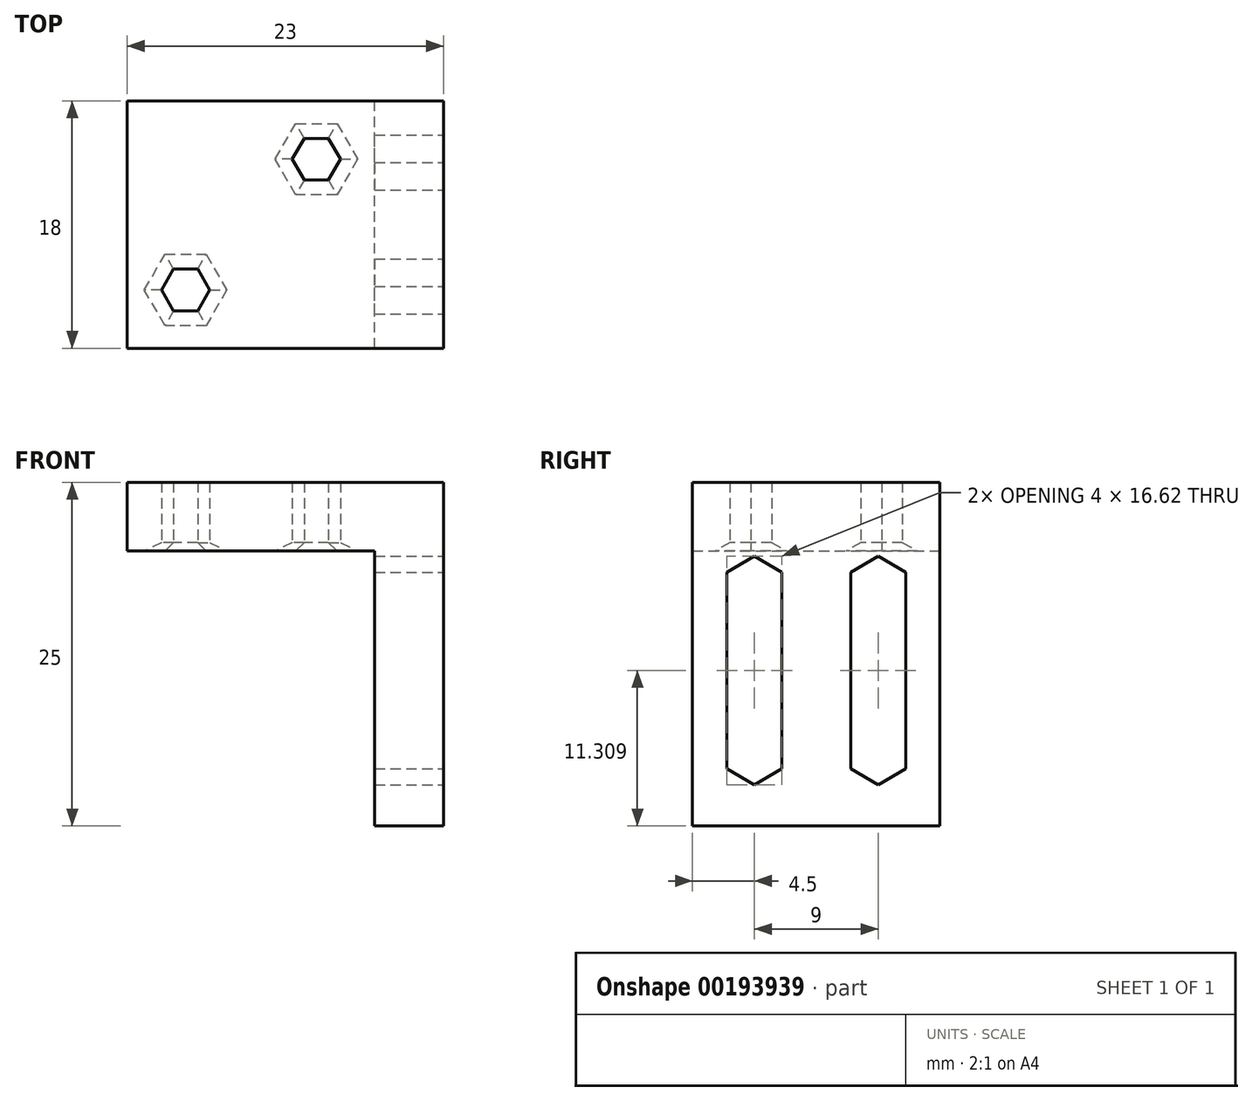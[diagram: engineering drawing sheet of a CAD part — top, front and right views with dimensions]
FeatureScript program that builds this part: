
annotation { "Feature Type Name" : "Feature", "Feature Type Description" : "" }
export const myFeature = defineFeature(function(context is Context, id is Id, definition is map)
    precondition{}
    {
        {
            var Q0;
            Q0=qCreatedBy(makeId("Front.planeOp"),FACE);
            var sketch = newSketch(context, id + "F0", { "sketchPlane" : qUnion([Q0])});
            skLineSegment(sketch, "E0", {"start": v(0, 0) * mm, "end": v(0, 20) * mm});
            skLineSegment(sketch, "E1", {"start": v(0, 20) * mm, "end": v(-18, 20) * mm});
            skLineSegment(sketch, "E2", {"start": v(-18, 20) * mm, "end": v(-18, 25) * mm});
            skLineSegment(sketch, "E3", {"start": v(-18, 25) * mm, "end": v(5, 25) * mm});
            skLineSegment(sketch, "E4", {"start": v(5, 25) * mm, "end": v(5, 0) * mm});
            skLineSegment(sketch, "E5", {"start": v(5, 0) * mm, "end": v(0, 0) * mm});
            skSolve(sketch);
        }
        {
            var Q0;
            Q0 = qSketchRegion(id + "F0", true);
            extrude(context, id + "F1", {"entities" : qUnion([Q0]), "depth" : 18 * mm});
        }
        {
            var Q0;
            Q0=makeQuery(id+"F1.opExtrude","SWEPT_FACE",FACE,{"disambiguationData":[OSD([sQuery(id+"F0.wireOp",EDGE,"E4")])]});
            var sketch = newSketch(context, id + "F2", { "sketchPlane" : qUnion([Q0])});
            skLineSegment(sketch, "E6", {"start": v(-9, 25) * mm, "end": v(-9, 0) * mm, "construction": true});
            skLineSegment(sketch, "E7", {"start": v(-13.5, 17.3) * mm, "end": v(-13.5, 5.3) * mm, "construction": true});
            skLineSegment(sketch, "E8", {"start": v(-18, 12.5) * mm, "end": v(-9, 12.5) * mm, "construction": true});
            skPoint(sketch, "E9", {"position": v(-13.5, 12.5) * mm});
            skCircle(sketch, "E10.cCircle", {"center": v(-13.5, 17.3) * mm, "radius": 2.3 * mm, "construction": true});
            skLineSegment(sketch, "E10.0", {"start": v(-13.5, 19.62) * mm, "end": v(-11.5, 18.46) * mm});
            skLineSegment(sketch, "E10.1", {"start": v(-11.5, 18.46) * mm, "end": v(-11.5, 16.15) * mm});
            skLineSegment(sketch, "E10.4", {"start": v(-15.5, 16.15) * mm, "end": v(-15.5, 18.46) * mm});
            skLineSegment(sketch, "E10.5", {"start": v(-15.5, 18.46) * mm, "end": v(-13.5, 19.62) * mm});
            skCircle(sketch, "E11.cCircle", {"center": v(-13.5, 5.3) * mm, "radius": 2.3 * mm, "construction": true});
            skLineSegment(sketch, "E11.0", {"start": v(-13.5, 3) * mm, "end": v(-15.5, 4.15) * mm});
            skLineSegment(sketch, "E11.1", {"start": v(-15.5, 4.15) * mm, "end": v(-15.5, 6.46) * mm});
            skLineSegment(sketch, "E11.4", {"start": v(-11.5, 6.46) * mm, "end": v(-11.5, 4.15) * mm});
            skLineSegment(sketch, "E11.5", {"start": v(-11.5, 4.15) * mm, "end": v(-13.5, 3) * mm});
            skLineSegment(sketch, "E12", {"start": v(-15.5, 16.15) * mm, "end": v(-15.5, 6.46) * mm});
            skLineSegment(sketch, "E13", {"start": v(-11.5, 16.15) * mm, "end": v(-11.5, 6.46) * mm});
            skLineSegment(sketch, "E14.MirrorCS", {"start": v(-15.5, 18.46) * mm, "end": v(-15.5, 16.15) * mm});
            skLineSegment(sketch, "E15.MirrorCS", {"start": v(-13.5, 19.62) * mm, "end": v(-15.5, 18.46) * mm});
            skLineSegment(sketch, "E16.MirrorCS", {"start": v(-11.5, 16.15) * mm, "end": v(-11.5, 18.46) * mm});
            skLineSegment(sketch, "E17.MirrorCS", {"start": v(-13.5, 3) * mm, "end": v(-11.5, 4.15) * mm});
            skLineSegment(sketch, "E18.MirrorCS", {"start": v(-11.5, 4.15) * mm, "end": v(-11.5, 6.46) * mm});
            skLineSegment(sketch, "E19.MirrorCS", {"start": v(-15.5, 6.46) * mm, "end": v(-15.5, 4.15) * mm});
            skLineSegment(sketch, "E20.MirrorCS", {"start": v(-15.5, 4.15) * mm, "end": v(-13.5, 3) * mm});
            skLineSegment(sketch, "E21.MirrorCS", {"start": v(-11.5, 18.46) * mm, "end": v(-13.5, 19.62) * mm});
            skLineSegment(sketch, "E22.MirrorCS", {"start": v(-2.5, 6.46) * mm, "end": v(-2.5, 4.15) * mm});
            skLineSegment(sketch, "E23.MirrorCS", {"start": v(-4.5, 3) * mm, "end": v(-2.5, 4.15) * mm});
            skLineSegment(sketch, "E24.MirrorCS", {"start": v(-4.5, 3) * mm, "end": v(-6.5, 4.15) * mm});
            skLineSegment(sketch, "E25.MirrorCS", {"start": v(-6.5, 4.15) * mm, "end": v(-6.5, 6.46) * mm});
            skLineSegment(sketch, "E26.MirrorCS", {"start": v(-6.5, 16.15) * mm, "end": v(-6.5, 6.46) * mm});
            skLineSegment(sketch, "E27.MirrorCS", {"start": v(-6.5, 18.46) * mm, "end": v(-6.5, 16.15) * mm});
            skLineSegment(sketch, "E28.MirrorCS", {"start": v(-4.5, 19.62) * mm, "end": v(-6.5, 18.46) * mm});
            skLineSegment(sketch, "E29.MirrorCS", {"start": v(-4.5, 19.62) * mm, "end": v(-2.5, 18.46) * mm});
            skLineSegment(sketch, "E30.MirrorCS", {"start": v(-2.5, 16.15) * mm, "end": v(-2.5, 6.46) * mm});
            skLineSegment(sketch, "E31.MirrorCS", {"start": v(-2.5, 16.15) * mm, "end": v(-2.5, 18.46) * mm});
            skSolve(sketch);
        }
        {
            var Q0;
            Q0 = qSketchRegion(id + "F2", true);
            extrude(context, id + "F3", {"entities" : qUnion([Q0]), "operationType" : NewBodyOperationType.REMOVE, "endBound" : BoundingType.UP_TO_NEXT, "oppositeDirection" : true, "depth" : 25 * mm});
        }
        {
            var Q0;
            Q0=makeQuery(id+"F1.opExtrude","SWEPT_FACE",FACE,{"disambiguationData":[OSD([sQuery(id+"F0.wireOp",EDGE,"E1")])]});
            var sketch = newSketch(context, id + "F4", { "sketchPlane" : qUnion([Q0])});
            skLineSegment(sketch, "E32", {"start": v(-18, 18) * mm, "end": v(0, 0) * mm, "construction": true});
            skCircle(sketch, "E33.cCircle", {"center": v(-13.76, 13.76) * mm, "radius": 3 * mm, "construction": true});
            skLineSegment(sketch, "E33.0", {"start": v(-10.76, 13.76) * mm, "end": v(-12.26, 11.16) * mm});
            skLineSegment(sketch, "E33.1", {"start": v(-12.26, 11.16) * mm, "end": v(-15.26, 11.16) * mm});
            skLineSegment(sketch, "E33.2", {"start": v(-15.26, 11.16) * mm, "end": v(-16.76, 13.76) * mm});
            skLineSegment(sketch, "E33.3", {"start": v(-16.76, 13.76) * mm, "end": v(-15.26, 16.36) * mm});
            skLineSegment(sketch, "E33.4", {"start": v(-15.26, 16.36) * mm, "end": v(-12.26, 16.36) * mm});
            skLineSegment(sketch, "E33.5", {"start": v(-12.26, 16.36) * mm, "end": v(-10.76, 13.76) * mm});
            skCircle(sketch, "E34.cCircle", {"center": v(-4.24, 4.24) * mm, "radius": 3 * mm, "construction": true});
            skLineSegment(sketch, "E34.0", {"start": v(-1.24, 4.24) * mm, "end": v(-2.74, 1.64) * mm});
            skLineSegment(sketch, "E34.1", {"start": v(-2.74, 1.64) * mm, "end": v(-5.74, 1.64) * mm});
            skLineSegment(sketch, "E34.2", {"start": v(-5.74, 1.64) * mm, "end": v(-7.24, 4.24) * mm});
            skLineSegment(sketch, "E34.3", {"start": v(-7.24, 4.24) * mm, "end": v(-5.74, 6.84) * mm});
            skLineSegment(sketch, "E34.4", {"start": v(-5.74, 6.84) * mm, "end": v(-2.74, 6.84) * mm});
            skLineSegment(sketch, "E34.5", {"start": v(-2.74, 6.84) * mm, "end": v(-1.24, 4.24) * mm});
            skSolve(sketch);
        }
        {
            var Q0;
            Q0 = qSketchRegion(id + "F4", true);
            extrude(context, id + "F5", {"entities" : qUnion([Q0]), "operationType" : NewBodyOperationType.REMOVE, "endBound" : BoundingType.UP_TO_NEXT, "oppositeDirection" : true, "depth" : 25 * mm, "hasDraft" : true, "draftAngle" : 60 * degree, "draftPullDirection" : true});
        }
        {
            var Q0;
            Q0=makeQuery(id+"F1.opExtrude","SWEPT_FACE",FACE,{"disambiguationData":[OSD([sQuery(id+"F0.wireOp",EDGE,"E1")])]});
            var sketch = newSketch(context, id + "F6", { "sketchPlane" : qUnion([Q0])});
            skCircle(sketch, "E35.cCircle", {"center": v(-13.76, 13.76) * mm, "radius": 1.75 * mm, "construction": true});
            skLineSegment(sketch, "E35.0", {"start": v(-12, 13.76) * mm, "end": v(-12.88, 12.24) * mm});
            skLineSegment(sketch, "E35.1", {"start": v(-12.88, 12.24) * mm, "end": v(-14.63, 12.24) * mm});
            skLineSegment(sketch, "E35.2", {"start": v(-14.63, 12.24) * mm, "end": v(-15.5, 13.76) * mm});
            skLineSegment(sketch, "E35.3", {"start": v(-15.5, 13.76) * mm, "end": v(-14.63, 15.27) * mm});
            skLineSegment(sketch, "E35.4", {"start": v(-14.63, 15.27) * mm, "end": v(-12.88, 15.27) * mm});
            skLineSegment(sketch, "E35.5", {"start": v(-12.88, 15.27) * mm, "end": v(-12, 13.76) * mm});
            skCircle(sketch, "E36.cCircle", {"center": v(-4.24, 4.24) * mm, "radius": 1.75 * mm, "construction": true});
            skLineSegment(sketch, "E36.0", {"start": v(-3.37, 5.76) * mm, "end": v(-2.5, 4.24) * mm});
            skLineSegment(sketch, "E36.1", {"start": v(-2.5, 4.24) * mm, "end": v(-3.37, 2.73) * mm});
            skLineSegment(sketch, "E36.2", {"start": v(-3.37, 2.73) * mm, "end": v(-5.12, 2.73) * mm});
            skLineSegment(sketch, "E36.3", {"start": v(-5.12, 2.73) * mm, "end": v(-6, 4.24) * mm});
            skLineSegment(sketch, "E36.4", {"start": v(-6, 4.24) * mm, "end": v(-5.12, 5.76) * mm});
            skLineSegment(sketch, "E36.5", {"start": v(-5.12, 5.76) * mm, "end": v(-3.37, 5.76) * mm});
            skSolve(sketch);
        }
        {
            var Q0;
            Q0 = qSketchRegion(id + "F6", true);
            extrude(context, id + "F7", {"entities" : qUnion([Q0]), "operationType" : NewBodyOperationType.REMOVE, "endBound" : BoundingType.THROUGH_ALL, "oppositeDirection" : true, "depth" : 25 * mm});
        }
    });
